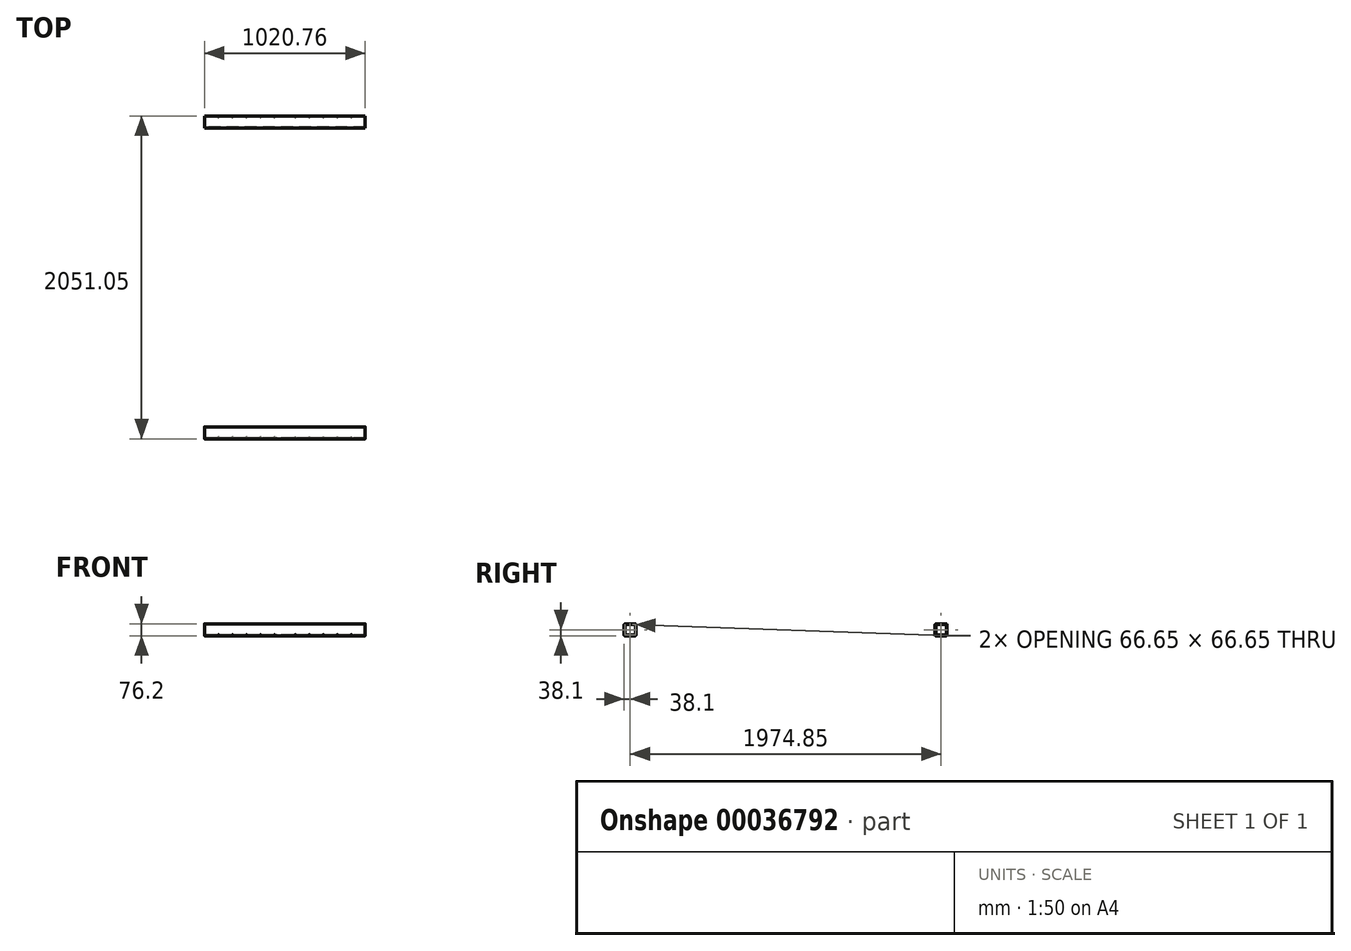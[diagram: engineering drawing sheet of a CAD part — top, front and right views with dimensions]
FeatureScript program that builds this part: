
annotation { "Feature Type Name" : "Feature", "Feature Type Description" : "" }
export const myFeature = defineFeature(function(context is Context, id is Id, definition is map)
    precondition{}
    {
        {
            var Q0;
            Q0=qCreatedBy(makeId("Right.planeOp"),FACE);
            var sketch = newSketch(context, id + "F0", { "sketchPlane" : qUnion([Q0])});
            skCircle(sketch, "E0.cCircle", {"center": v(0, 1104.9) * mm, "radius": 38.1 * mm, "construction": true});
            skLineSegment(sketch, "E0.0", {"start": v(-38.1, 1073.15) * mm, "end": v(-38.1, 1136.65) * mm});
            skLineSegment(sketch, "E0.1", {"start": v(-31.75, 1143) * mm, "end": v(31.75, 1143) * mm});
            skLineSegment(sketch, "E0.2", {"start": v(38.1, 1136.65) * mm, "end": v(38.1, 1073.15) * mm});
            skLineSegment(sketch, "E0.3", {"start": v(31.75, 1066.8) * mm, "end": v(-31.75, 1066.8) * mm});
            skPoint(sketch, "E0.0.midPoint", {"position": v(-38.1, 1104.9) * mm});
            skPoint(sketch, "E1.visualSharp", {"position": v(-38.1, 1143) * mm});
            skArc(sketch, "E1.filletArc", {"start": v(-31.75, 1143) * mm, "mid": v(-36.24, 1141.14) * mm, "end": v(-38.1, 1136.65) * mm});
            skPoint(sketch, "E2.visualSharp", {"position": v(38.1, 1143) * mm});
            skArc(sketch, "E2.filletArc", {"start": v(38.1, 1136.65) * mm, "mid": v(36.24, 1141.14) * mm, "end": v(31.75, 1143) * mm});
            skPoint(sketch, "E3.visualSharp", {"position": v(38.1, 1066.8) * mm});
            skArc(sketch, "E3.filletArc", {"start": v(31.75, 1066.8) * mm, "mid": v(36.24, 1068.66) * mm, "end": v(38.1, 1073.15) * mm});
            skPoint(sketch, "E4.visualSharp", {"position": v(-38.1, 1066.8) * mm});
            skArc(sketch, "E4.filletArc", {"start": v(-38.1, 1073.15) * mm, "mid": v(-36.24, 1068.66) * mm, "end": v(-31.75, 1066.8) * mm});
            skLineSegment(sketch, "E5.0", {"start": v(-33.32, 1077.93) * mm, "end": v(-33.32, 1131.87) * mm});
            skLineSegment(sketch, "E5.1", {"start": v(26.97, 1071.58) * mm, "end": v(-26.97, 1071.58) * mm});
            skLineSegment(sketch, "E5.2", {"start": v(33.32, 1131.87) * mm, "end": v(33.32, 1077.93) * mm});
            skLineSegment(sketch, "E5.3", {"start": v(-26.97, 1138.22) * mm, "end": v(26.97, 1138.22) * mm});
            skPoint(sketch, "E6.visualSharp", {"position": v(-33.32, 1138.22) * mm});
            skArc(sketch, "E6.filletArc", {"start": v(-26.97, 1138.22) * mm, "mid": v(-31.46, 1136.36) * mm, "end": v(-33.32, 1131.87) * mm});
            skPoint(sketch, "E7.visualSharp", {"position": v(33.32, 1138.22) * mm});
            skArc(sketch, "E7.filletArc", {"start": v(33.32, 1131.87) * mm, "mid": v(31.46, 1136.36) * mm, "end": v(26.97, 1138.22) * mm});
            skPoint(sketch, "E8.visualSharp", {"position": v(-33.32, 1071.58) * mm});
            skArc(sketch, "E8.filletArc", {"start": v(-33.32, 1077.93) * mm, "mid": v(-31.46, 1073.44) * mm, "end": v(-26.97, 1071.58) * mm});
            skPoint(sketch, "E9.visualSharp", {"position": v(33.32, 1071.58) * mm});
            skArc(sketch, "E9.filletArc", {"start": v(26.97, 1071.58) * mm, "mid": v(31.46, 1073.44) * mm, "end": v(33.32, 1077.93) * mm});
            skSolve(sketch);
        }
        {
            var Q0;
            Q0=makeQuery(id+"F0.imprint","IMPRINT",FACE,{"disambiguationData":[TD([[makeQuery(id+"F0.imprint","IMPRINT",EDGE,{"derivedFrom":sQuery(id+"F0.wireOp",EDGE,"E0.0")}),-1.0]])]});
            extrude(context, id + "F1", {"entities" : qUnion([Q0]), "depth" : 1020.76 * mm});
        }
        {
            var Q0;
            Q0=makeQuery(id+"F1.opExtrude","CAP_VERTEX",VERTEX,{"disambiguationData":[OSD([sQuery(id+"F0.wireOp",EDGE,"E0.0"),sQuery(id+"F0.wireOp",EDGE,"E4.filletArc")])],"isStart":true});
            var Q1;
            Q1=makeQuery(id+"F1.opExtrude","CAP_VERTEX",VERTEX,{"disambiguationData":[OSD([sQuery(id+"F0.wireOp",EDGE,"E0.3"),sQuery(id+"F0.wireOp",EDGE,"E4.filletArc")])],"isStart":true});
            var Q2;
            Q2=makeQuery(id+"F1.opExtrude","CAP_VERTEX",VERTEX,{"disambiguationData":[OSD([sQuery(id+"F0.wireOp",EDGE,"E0.3"),sQuery(id+"F0.wireOp",EDGE,"E4.filletArc")])],"isStart":false});
            cPlane(context, id + "F2", {"entities" : qUnion([Q0, Q1, Q2]), "cplaneType" : CPlaneType.THREE_POINT, "offset" : 152.4 * mm, "width" : 152.4 * mm, "height" : 152.4 * mm});
        }
        {
            var Q0;
            Q0=qCreatedBy(id+"F2.planeOp",FACE);
            var sketch = newSketch(context, id + "F3", { "sketchPlane" : qUnion([Q0])});
            skLineSegment(sketch, "E10", {"start": v(0, 758.49) * mm, "end": v(0, 794.72) * mm});
            skLineSegment(sketch, "E11", {"start": v(0, 785.72) * mm, "end": v(2.15, 785.72) * mm});
            skLineSegment(sketch, "E12", {"start": v(0.5, 776.82) * mm, "end": v(3.25, 776.82) * mm});
            skCircle(sketch, "E13", {"center": v(-88.9, 781.31) * mm, "radius": 4.76 * mm});
            skCircle(sketch, "E14.1.0.0", {"center": v(-177.8, 781.31) * mm, "radius": 4.76 * mm});
            skCircle(sketch, "E14.2.0.0", {"center": v(-266.7, 781.31) * mm, "radius": 4.76 * mm});
            skCircle(sketch, "E14.3.0.0", {"center": v(-355.6, 781.31) * mm, "radius": 4.76 * mm});
            skLineSegment(sketch, "E14.direction1", {"start": v(-88.9, 781.31) * mm, "end": v(-177.8, 781.31) * mm, "construction": true});
            skCircle(sketch, "E15.0.4.0", {"center": v(-444.5, 781.31) * mm, "radius": 4.76 * mm});
            skCircle(sketch, "E16.1.0.0", {"center": v(-576.26, 781.31) * mm, "radius": 4.76 * mm});
            skLineSegment(sketch, "E16.direction1", {"start": v(-444.5, 781.31) * mm, "end": v(-576.26, 781.31) * mm, "construction": true});
            skCircle(sketch, "E17.1.0.0", {"center": v(-665.16, 781.31) * mm, "radius": 4.76 * mm});
            skCircle(sketch, "E17.2.0.0", {"center": v(-754.06, 781.31) * mm, "radius": 4.76 * mm});
            skCircle(sketch, "E17.3.0.0", {"center": v(-842.96, 781.31) * mm, "radius": 4.76 * mm});
            skCircle(sketch, "E17.4.0.0", {"center": v(-931.86, 781.31) * mm, "radius": 4.76 * mm});
            skLineSegment(sketch, "E17.direction1", {"start": v(-576.26, 781.31) * mm, "end": v(-665.16, 781.31) * mm, "construction": true});
            skSolve(sketch);
        }
        {
            var Q0;
            Q0 = qSketchRegion(id + "F3", true);
            extrude(context, id + "F4", {"entities" : qUnion([Q0]), "operationType" : NewBodyOperationType.REMOVE, "endBound" : BoundingType.SYMMETRIC, "oppositeDirection" : true, "depth" : 25.4 * mm});
        }
        {
            var Q0;
            Q0=qCreatedBy(makeId("Front.planeOp"),FACE);
            cPlane(context, id + "F5", {"entities" : qUnion([Q0]), "cplaneType" : CPlaneType.OFFSET, "offset" : 987.42 * mm, "oppositeDirection" : true, "width" : 152.4 * mm, "height" : 152.4 * mm});
        }
        {
            var Q0;
            Q0=makeQuery(id+"F1.opExtrude","SWEPT_BODY",BODY,{"disambiguationData":[OSD([sQuery(id+"F0.wireOp",EDGE,"E0.0"),sQuery(id+"F0.wireOp",EDGE,"E0.1"),sQuery(id+"F0.wireOp",EDGE,"E0.2"),sQuery(id+"F0.wireOp",EDGE,"E0.3"),sQuery(id+"F0.wireOp",EDGE,"E1.filletArc"),sQuery(id+"F0.wireOp",EDGE,"E2.filletArc"),sQuery(id+"F0.wireOp",EDGE,"E3.filletArc"),sQuery(id+"F0.wireOp",EDGE,"E4.filletArc"),sQuery(id+"F0.wireOp",EDGE,"E5.0"),sQuery(id+"F0.wireOp",EDGE,"E5.1"),sQuery(id+"F0.wireOp",EDGE,"E5.2"),sQuery(id+"F0.wireOp",EDGE,"E5.3"),sQuery(id+"F0.wireOp",EDGE,"E6.filletArc"),sQuery(id+"F0.wireOp",EDGE,"E7.filletArc"),sQuery(id+"F0.wireOp",EDGE,"E8.filletArc"),sQuery(id+"F0.wireOp",EDGE,"E9.filletArc")])]});
            var Q1;
            Q1=qCreatedBy(id+"F5.planeOp",FACE);
            mirror(context, id + "F6", {"entities" : qUnion([Q0]), "mirrorPlane" : qUnion([Q1])});
        }
    });
